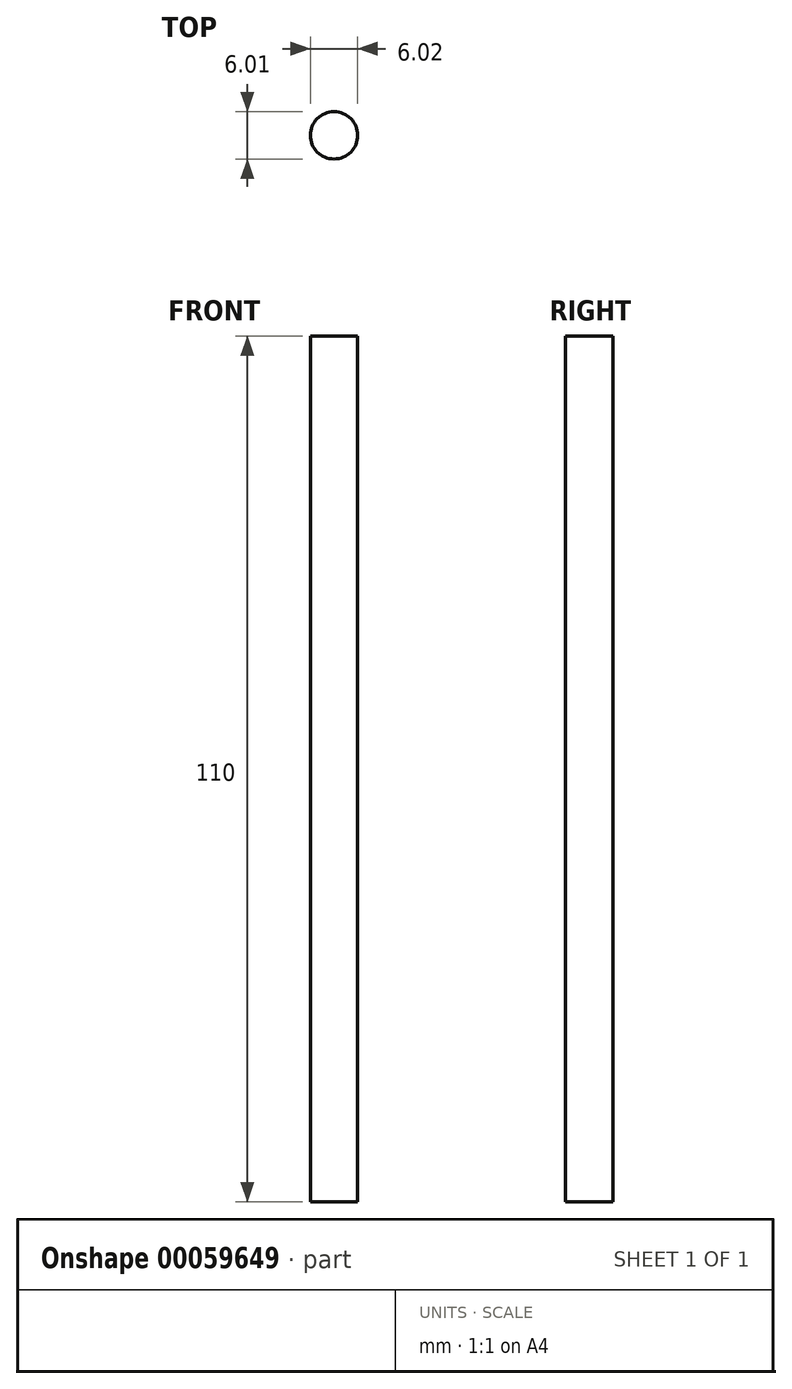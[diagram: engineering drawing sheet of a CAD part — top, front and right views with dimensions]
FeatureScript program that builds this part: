
annotation { "Feature Type Name" : "Feature", "Feature Type Description" : "" }
export const myFeature = defineFeature(function(context is Context, id is Id, definition is map)
    precondition{}
    {
        {
            var Q0;
            Q0=qCreatedBy(makeId("Top.planeOp"),FACE);
            var sketch = newSketch(context, id + "F0", { "sketchPlane" : qUnion([Q0])});
            skCircle(sketch, "E0", {"center": v(-47.12, 30.89) * mm, "radius": 3 * mm});
            skSolve(sketch);
        }
        {
            var Q0;
            Q0 = qSketchRegion(id + "F0", true);
            extrude(context, id + "F1", {"entities" : qUnion([Q0]), "depth" : 110 * mm});
        }
    });
